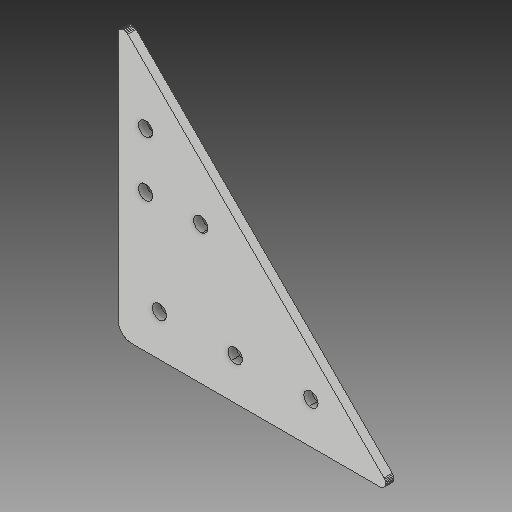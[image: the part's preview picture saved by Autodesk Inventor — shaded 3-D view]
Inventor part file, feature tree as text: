
AUTODESK INVENTOR PART (.ipt)
format: ipt  version: 2018 (Build 220112000, 112)  size: 231,424 bytes
history: native  units: mm
features: other x3, sketch x2, hole x1, projected_geometry x1
ambient origin geometry x8: Origin, YZ Plane, XZ Plane, XY Plane, X Axis, Y Axis, Z Axis, Center Point
bodies: Solid1 (feature_tree)
feature tree (7):
  other  "Side Brace.ipt"
  hole  "Hole1"  [1 undecoded]
  other  "Solid1::Side Brace.ipt"
  other  "TaggingFeature1"
  sketch  "Sketch1"  dims[d0=10.0mm]
  sketch  "Sketch2"  dims[d1=5.2mm d2=6.0mm d3=4.0mm d4=2.0mm d5=90.0deg d6=8.0mm d7=20.594885mm]
  projected_geometry  "Projected Loop1"
note: 1 required parameter value undecoded (feature->parameter linkage not recoverable at this tier; creation-order binding heuristic only, values carry confidence <= 0.55)
